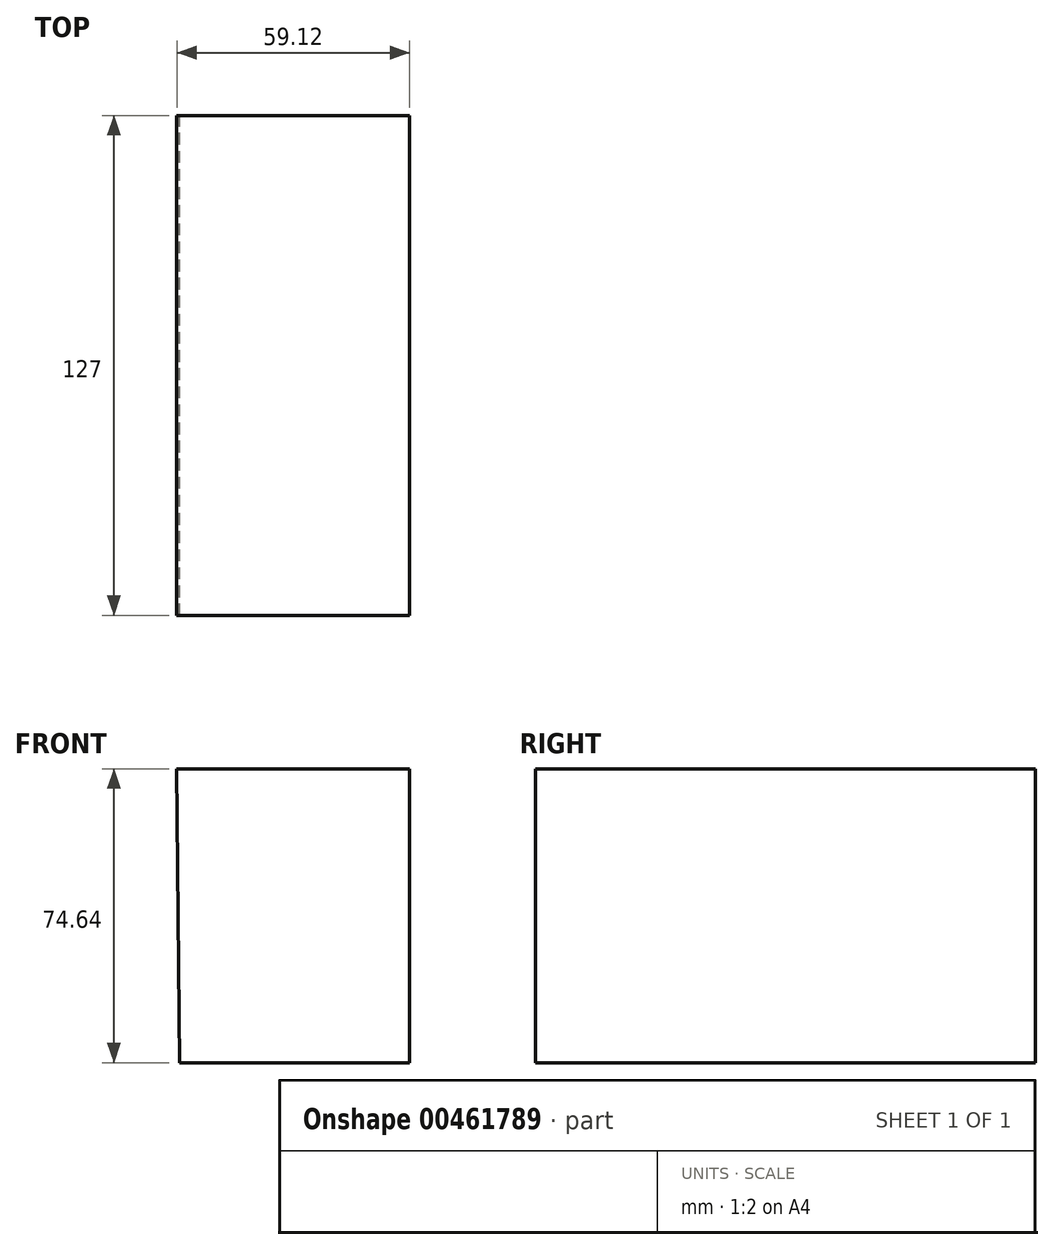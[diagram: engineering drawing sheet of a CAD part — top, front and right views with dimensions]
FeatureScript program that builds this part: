
annotation { "Feature Type Name" : "Feature", "Feature Type Description" : "" }
export const myFeature = defineFeature(function(context is Context, id is Id, definition is map)
    precondition{}
    {
        {
            var Q0;
            Q0=qCreatedBy(makeId("Front.planeOp"),FACE);
            var sketch = newSketch(context, id + "F0", { "sketchPlane" : qUnion([Q0])});
            skLineSegment(sketch, "E0", {"start": v(-30.3, 45.45) * mm, "end": v(28.82, 45.45) * mm});
            skLineSegment(sketch, "E1", {"start": v(28.82, 45.45) * mm, "end": v(28.82, -29.2) * mm});
            skLineSegment(sketch, "E2", {"start": v(28.82, -29.2) * mm, "end": v(-29.56, -29.2) * mm});
            skLineSegment(sketch, "E3", {"start": v(-29.56, -29.2) * mm, "end": v(-30.3, 45.45) * mm});
            skSolve(sketch);
        }
        {
            var Q0;
            Q0=makeQuery(id+"F0.imprint","IMPRINT",FACE,{"disambiguationData":[TD([[makeQuery(id+"F0.imprint","IMPRINT",EDGE,{"derivedFrom":sQuery(id+"F0.wireOp",EDGE,"E0")}),-1.0]])]});
            var Q1;
            Q1 = qSketchRegion(id + "F0", true);
            extrude(context, id + "F1", {"entities" : qUnion([Q0, Q1]), "depth" : 127 * mm});
        }
        {
            var Q0;
            Q0=makeQuery(id+"F1.opExtrude","CAP_FACE",FACE,{"disambiguationData":[OSD([sQuery(id+"F0.wireOp",EDGE,"E0"),sQuery(id+"F0.wireOp",EDGE,"E1"),sQuery(id+"F0.wireOp",EDGE,"E2"),sQuery(id+"F0.wireOp",EDGE,"E3")])],"isStart":false});
            var sketch = newSketch(context, id + "F2", { "sketchPlane" : qUnion([Q0])});
            skCircle(sketch, "E4", {"center": v(0, 0) * mm, "radius": 14.12 * mm});
            skCircle(sketch, "E5", {"center": v(0, 0) * mm, "radius": 17.44 * mm});
            skSolve(sketch);
        }
        {
            var Q0;
            Q0=makeQuery(id+"F2.imprint","IMPRINT",FACE,{"disambiguationData":[TD([[makeQuery(id+"F2.imprint","IMPRINT",EDGE,{"derivedFrom":sQuery(id+"F2.wireOp",EDGE,"E5")}),-1.0]])]});
            var Q1;
            Q1=sQuery(id+"F2.wireOp",EDGE,"E4");
            extrude(context, id + "F3", {"entities" : qUnion([Q0]), "operationType" : NewBodyOperationType.REMOVE, "surfaceEntities" : qUnion([Q1]), "depth" : 127 * mm});
        }
    });
